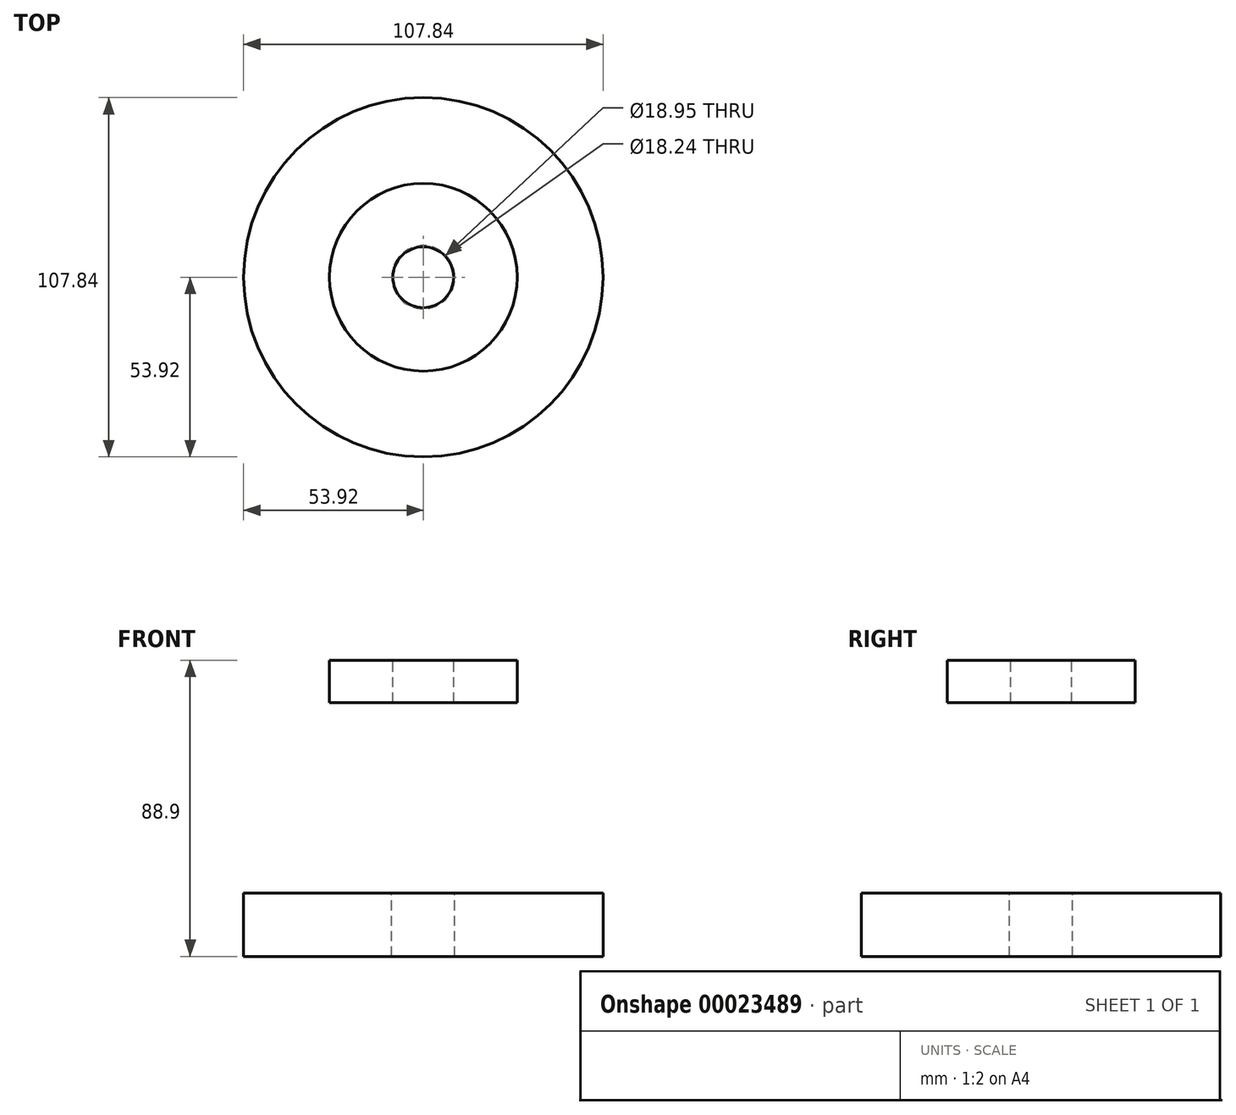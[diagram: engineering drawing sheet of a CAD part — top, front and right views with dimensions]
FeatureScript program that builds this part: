
annotation { "Feature Type Name" : "Feature", "Feature Type Description" : "" }
export const myFeature = defineFeature(function(context is Context, id is Id, definition is map)
    precondition{}
    {
        {
            var Q0;
            Q0=qCreatedBy(makeId("Front.planeOp"),FACE);
            var sketch = newSketch(context, id + "F0", { "sketchPlane" : qUnion([Q0])});
            skLineSegment(sketch, "E0.bottom", {"start": v(9.47, -23.55) * mm, "end": v(53.92, -23.55) * mm});
            skLineSegment(sketch, "E0.top", {"start": v(9.47, -42.6) * mm, "end": v(53.92, -42.6) * mm});
            skLineSegment(sketch, "E0.left", {"start": v(9.47, -23.55) * mm, "end": v(9.47, -42.6) * mm});
            skLineSegment(sketch, "E0.right", {"start": v(53.92, -23.55) * mm, "end": v(53.92, -42.6) * mm});
            skLineSegment(sketch, "E1.bottom", {"start": v(9.53, -23.55) * mm, "end": v(34.93, -23.55) * mm});
            skLineSegment(sketch, "E1.top", {"start": v(9.52, 33.6) * mm, "end": v(34.92, 33.6) * mm});
            skLineSegment(sketch, "E1.left", {"start": v(9.53, -23.55) * mm, "end": v(9.52, 33.6) * mm});
            skLineSegment(sketch, "E1.right", {"start": v(34.93, -23.55) * mm, "end": v(34.92, 33.6) * mm});
            skLineSegment(sketch, "E2.bottom", {"start": v(9.12, 33.6) * mm, "end": v(28.17, 33.6) * mm});
            skLineSegment(sketch, "E2.top", {"start": v(9.12, 46.3) * mm, "end": v(28.17, 46.3) * mm});
            skLineSegment(sketch, "E2.left", {"start": v(9.12, 33.6) * mm, "end": v(9.12, 46.3) * mm});
            skLineSegment(sketch, "E2.right", {"start": v(28.17, 33.6) * mm, "end": v(28.17, 46.3) * mm});
            skLineSegment(sketch, "E3", {"start": v(0, 0) * mm, "end": v(0, 30.36) * mm, "construction": true});
            skLineSegment(sketch, "E4", {"start": v(0, 0) * mm, "end": v(0, -27.66) * mm, "construction": true});
            skSolve(sketch);
        }
        {
            var Q0;
            Q0=makeQuery(id+"F0.imprint","IMPRINT",FACE,{"disambiguationData":[TD([[makeQuery(id+"F0.imprint","IMPRINT",EDGE,{"derivedFrom":sQuery(id+"F0.wireOp",EDGE,"E2.bottom")}),1.0]])]});
            var Q1;
            Q1=makeQuery(id+"F0.imprint","IMPRINT",FACE,{"disambiguationData":[TD([[makeQuery(id+"F0.imprint","IMPRINT",EDGE,{"derivedFrom":sQuery(id+"F0.wireOp",EDGE,"E1.bottom")}),1.0]])]});
            var Q2;
            Q2=makeQuery(id+"F0.imprint","IMPRINT",FACE,{"disambiguationData":[TD([[makeQuery(id+"F0.imprint","IMPRINT",EDGE,{"derivedFrom":sQuery(id+"F0.wireOp",EDGE,"E0.top")}),1.0]])]});
            var Q3;
            Q3=sQuery(id+"F0.wireOp",EDGE,"E4");
            revolve(context, id + "F1", {"entities" : qUnion([Q0, Q1, Q2]), "axis" : qUnion([Q3]), "revolveType" : RevolveType.FULL});
        }
    });
